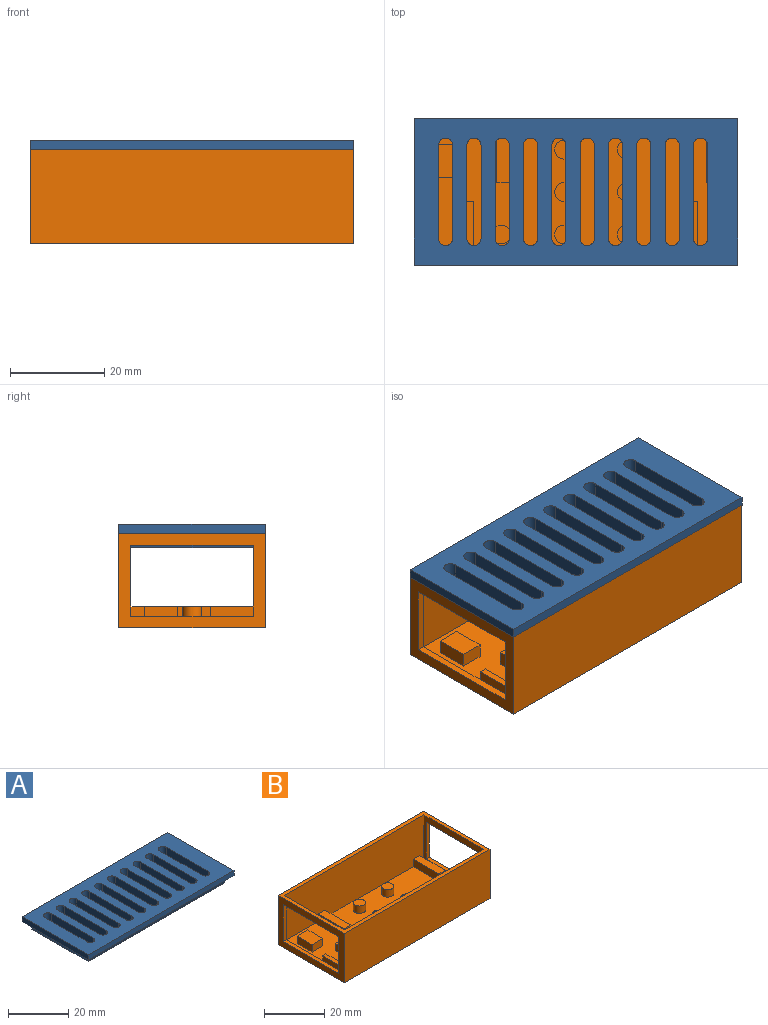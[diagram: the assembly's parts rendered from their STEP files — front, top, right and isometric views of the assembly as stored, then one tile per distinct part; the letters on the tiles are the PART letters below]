
ASSEMBLY  parts=2 mates=1
PART A: 51 faces, bbox 68.5x31x5 mm
  f0: plane 68.5x31mm, normal (0,0,1), area 1458.8mm2, adj f3,f4,f5,f6,f11,f12,f13,f14
  f1: plane 63.89x26.39mm, normal (0,0,-1), area 1021.5mm2, adj f7,f8,f9,f10,f11,f12,f13,f14
  f2: plane 68.5x31mm, normal (0,0,-1), area 289.5mm2, adj f3,f4,f5,f6,f7,f8,f9,f10
  f3: plane 68.5x2mm, normal (0,1,0), area 137mm2, adj f0,f2,f4,f6
  f4: plane 31x2mm, normal (-1,0,0), area 62mm2, adj f0,f2,f3,f5
  f5: plane 68.5x2mm, normal (0,-1,0), area 137mm2, adj f0,f2,f4,f6
  f6: plane 31x2mm, normal (1,0,0), area 62mm2, adj f0,f2,f3,f5
  f7: plane 28x3mm, normal (0.97,0,-0.26), area 84.5mm2, adj f1,f2,f8,f10
  f8: plane 65.5x3mm, normal (0,0.97,-0.26), area 200.9mm2, adj f1,f2,f7,f9
  f9: plane 28x3mm, normal (-0.97,0,-0.26), area 84.5mm2, adj f1,f2,f8,f10
  f10: plane 65.5x3mm, normal (0,-0.97,-0.26), area 200.9mm2, adj f1,f2,f7,f9
  f11: cylinder r=1.5mm len=5mm, axis (0,0,1), area 23.6mm2, adj f0,f1,f12,f14
  f12: plane 19.8x5mm, normal (-1,0,0), area 99mm2, adj f0,f1,f11,f13
  f13: cylinder r=1.5mm len=5mm, axis (0,0,1), area 23.6mm2, adj f0,f1,f12,f14
  f14: plane 19.8x5mm, normal (1,0,0), area 99mm2, adj f0,f1,f11,f13
  f15: cylinder r=1.5mm len=5mm, axis (0,0,1), area 23.6mm2, adj f0,f1,f16,f18
  f16: plane 19.8x5mm, normal (-1,0,0), area 99mm2, adj f0,f1,f15,f17
  f17: cylinder r=1.5mm len=5mm, axis (0,0,1), area 23.6mm2, adj f0,f1,f16,f18
  f18: plane 19.8x5mm, normal (1,0,0), area 99mm2, adj f0,f1,f15,f17
  f19: cylinder r=1.5mm len=5mm, axis (0,0,1), area 23.6mm2, adj f0,f1,f20,f22
  f20: plane 19.8x5mm, normal (-1,0,0), area 99mm2, adj f0,f1,f19,f21
  f21: cylinder r=1.5mm len=5mm, axis (0,0,1), area 23.6mm2, adj f0,f1,f20,f22
  f22: plane 19.8x5mm, normal (1,0,0), area 99mm2, adj f0,f1,f19,f21
  f23: cylinder r=1.5mm len=5mm, axis (0,0,1), area 23.6mm2, adj f0,f1,f24,f26
  f24: plane 19.8x5mm, normal (-1,0,0), area 99mm2, adj f0,f1,f23,f25
  f25: cylinder r=1.5mm len=5mm, axis (0,0,1), area 23.6mm2, adj f0,f1,f24,f26
  f26: plane 19.8x5mm, normal (1,0,0), area 99mm2, adj f0,f1,f23,f25
  f27: cylinder r=1.5mm len=5mm, axis (0,0,1), area 23.6mm2, adj f0,f1,f28,f30
  f28: plane 19.8x5mm, normal (-1,0,0), area 99mm2, adj f0,f1,f27,f29
  f29: cylinder r=1.5mm len=5mm, axis (0,0,1), area 23.6mm2, adj f0,f1,f28,f30
  f30: plane 19.8x5mm, normal (1,0,0), area 99mm2, adj f0,f1,f27,f29
  f31: cylinder r=1.5mm len=5mm, axis (0,0,1), area 23.6mm2, adj f0,f1,f32,f34
  f32: plane 19.8x5mm, normal (-1,0,0), area 99mm2, adj f0,f1,f31,f33
  f33: cylinder r=1.5mm len=5mm, axis (0,0,1), area 23.6mm2, adj f0,f1,f32,f34
  f34: plane 19.8x5mm, normal (1,0,0), area 99mm2, adj f0,f1,f31,f33
  f35: cylinder r=1.5mm len=5mm, axis (0,0,1), area 23.6mm2, adj f0,f1,f36,f38
  f36: plane 19.8x5mm, normal (-1,0,0), area 99mm2, adj f0,f1,f35,f37
  f37: cylinder r=1.5mm len=5mm, axis (0,0,1), area 23.6mm2, adj f0,f1,f36,f38
  f38: plane 19.8x5mm, normal (1,0,0), area 99mm2, adj f0,f1,f35,f37
  f39: cylinder r=1.5mm len=5mm, axis (0,0,1), area 23.6mm2, adj f0,f1,f40,f42
  f40: plane 19.8x5mm, normal (-1,0,0), area 99mm2, adj f0,f1,f39,f41
  f41: cylinder r=1.5mm len=5mm, axis (0,0,1), area 23.6mm2, adj f0,f1,f40,f42
  f42: plane 19.8x5mm, normal (1,0,0), area 99mm2, adj f0,f1,f39,f41
  f43: cylinder r=1.5mm len=5mm, axis (0,0,1), area 23.6mm2, adj f0,f1,f44,f46
  f44: plane 19.8x5mm, normal (-1,0,0), area 99mm2, adj f0,f1,f43,f45
  f45: cylinder r=1.5mm len=5mm, axis (0,0,1), area 23.6mm2, adj f0,f1,f44,f46
  f46: plane 19.8x5mm, normal (1,0,0), area 99mm2, adj f0,f1,f43,f45
  f47: plane 19.8x5mm, normal (1,0,0), area 99mm2, adj f0,f1,f48,f50
  f48: cylinder r=1.5mm len=5mm, axis (0,0,1), area 23.6mm2, adj f0,f1,f47,f49
  f49: plane 19.8x5mm, normal (-1,0,0), area 99mm2, adj f0,f1,f48,f50
  f50: cylinder r=1.5mm len=5mm, axis (0,0,1), area 23.6mm2, adj f0,f1,f47,f49
PART B: 58 faces, bbox 68.5x31x20 mm
  f0: plane 65.5x28mm, normal (0,0,1), area 1552mm2, adj f1,f4,f5,f10,f19,f20,f21,f23
  f1: plane 65.5x18.5mm, normal (0,-1,0), area 1193.7mm2, adj f0,f4,f5,f6,f19,f21,f22,f23
  f2: plane 31x20mm, normal (1,0,0), area 230mm2, adj f6,f7,f8,f9,f15,f16,f17,f18
  f3: plane 31x20mm, normal (-1,0,0), area 230mm2, adj f6,f7,f8,f9,f11,f12,f13,f14
  f4: plane 28x18.5mm, normal (-1,0,0), area 128mm2, adj f0,f1,f6,f10,f15,f16,f17,f18
  f5: plane 28x18.5mm, normal (1,0,0), area 116mm2, adj f0,f1,f6,f10,f11,f12,f13,f14
  f6: plane 68.5x31mm, normal (0,0,1), area 289.5mm2, adj f1,f2,f3,f4,f5,f7,f8,f10
  f7: plane 68.5x20mm, normal (0,1,0), area 1370mm2, adj f2,f3,f6,f9
  f8: plane 68.5x20mm, normal (0,-1,0), area 1370mm2, adj f2,f3,f6,f9
  f9: plane 68.5x31mm, normal (0,0,-1), area 2123.5mm2, adj f2,f3,f7,f8
  f10: plane 65.5x18.5mm, normal (0,1,0), area 1189.2mm2, adj f0,f4,f5,f6,f28,f29,f30,f50
  f11: plane 15x1.5mm, normal (0,-1,0), area 22.5mm2, adj f3,f5,f12,f14
  f12: plane 26x1.5mm, normal (0,0,1), area 39mm2, adj f3,f5,f11,f13,f56
  f13: plane 15x1.5mm, normal (0,1,0), area 22.5mm2, adj f3,f5,f12,f14,f56
  f14: plane 26x1.5mm, normal (0,0,-1), area 39mm2, adj f3,f5,f11,f13
  f15: plane 26x1.5mm, normal (0,0,-1), area 39mm2, adj f2,f4,f16,f18
  f16: plane 15x1.5mm, normal (0,1,0), area 22.5mm2, adj f2,f4,f15,f17
  f17: plane 26x1.5mm, normal (0,0,1), area 39mm2, adj f2,f4,f16,f18
  f18: plane 15x1.5mm, normal (0,-1,0), area 22.5mm2, adj f2,f4,f15,f17
  f19: plane 12x3mm, normal (-1,0,0), area 36mm2, adj f0,f1,f20,f22
  f20: plane 3x3mm, normal (0,-1,0), area 9mm2, adj f0,f19,f21,f22
  f21: plane 12x3mm, normal (1,0,0), area 36mm2, adj f0,f1,f20,f22
  f22: plane 12x3mm, normal (0,0,1), area 36mm2, adj f1,f19,f20,f21
  f23: plane 12x3mm, normal (-1,0,0), area 36mm2, adj f0,f1,f24,f26
  f24: plane 3x3mm, normal (0,-1,0), area 9mm2, adj f0,f23,f25,f26
  f25: plane 12x3mm, normal (1,0,0), area 36mm2, adj f0,f1,f24,f26
  f26: plane 12x3mm, normal (0,0,1), area 36mm2, adj f1,f23,f24,f25
  f27: plane 3x3mm, normal (0,1,0), area 9mm2, adj f0,f28,f29,f30
  f28: plane 12x3mm, normal (-1,0,0), area 36mm2, adj f0,f10,f27,f30
  f29: plane 12x3mm, normal (1,0,0), area 36mm2, adj f0,f10,f27,f30
  f30: plane 12x3mm, normal (0,0,1), area 36mm2, adj f10,f27,f28,f29
  f31: plane 5x3mm, normal (0,1,0), area 15mm2, adj f0,f32,f34,f35
  f32: plane 7x3mm, normal (-1,0,0), area 21mm2, adj f0,f31,f33,f35
  f33: plane 5x3mm, normal (0,-1,0), area 15mm2, adj f0,f32,f34,f35
  f34: plane 7x3mm, normal (1,0,0), area 21mm2, adj f0,f31,f33,f35
  f35: plane 7x5mm, normal (0,0,1), area 35mm2, adj f31,f32,f33,f34
  f36: cylinder r=2mm len=4mm, axis (0,0,-1), area 37.7mm2, adj f0,f37
  f37: plane 4x4mm, normal (0,0,1), area 12.6mm2, adj f36
  f38: cylinder r=2mm len=4mm, axis (0,0,-1), area 37.7mm2, adj f0,f39
  f39: plane 4x4mm, normal (0,0,1), area 12.6mm2, adj f38
  f40: cylinder r=2mm len=4mm, axis (0,0,-1), area 37.7mm2, adj f0,f41
  f41: plane 4x4mm, normal (0,0,1), area 12.6mm2, adj f40
  f42: cylinder r=2mm len=4mm, axis (0,0,-1), area 37.7mm2, adj f0,f43
  f43: plane 4x4mm, normal (0,0,1), area 12.6mm2, adj f42
  f44: cylinder r=2mm len=4mm, axis (0,0,-1), area 37.7mm2, adj f0,f45
  f45: plane 4x4mm, normal (0,0,1), area 12.6mm2, adj f44
  f46: cylinder r=2mm len=4mm, axis (0,0,-1), area 37.7mm2, adj f0,f47
  f47: plane 4x4mm, normal (0,0,1), area 12.6mm2, adj f46
  f48: cylinder r=2mm len=4mm, axis (0,0,-1), area 37.7mm2, adj f0,f49
  f49: plane 4x4mm, normal (0,0,1), area 12.6mm2, adj f48
  f50: plane 12x3mm, normal (1,0,0), area 36mm2, adj f0,f10,f51,f53
  f51: plane 3x3mm, normal (0,1,0), area 9mm2, adj f0,f50,f52,f53
  f52: plane 12x3mm, normal (-1,0,0), area 36mm2, adj f0,f10,f51,f53
  f53: plane 12x3mm, normal (0,0,1), area 36mm2, adj f10,f50,f51,f52
  f54: plane 10x3mm, normal (1,0,0), area 30mm2, adj f0,f10,f55,f57
  f55: plane 3x1.5mm, normal (0,1,0), area 4.5mm2, adj f0,f5,f54,f56,f57
  f56: plane 9x2mm, normal (-1,0,0), area 18mm2, adj f12,f13,f55,f57
  f57: plane 10x1.5mm, normal (0,0,1), area 15mm2, adj f5,f10,f54,f55,f56
PLACE A t=(-1.89,-5.48,16.5)mm
PLACE B t=(2.66,-2.56,-3.5)mm
MATE slider A.f2 <-> B.f6  axis (0,0,-1) through (-31.59,12.94,16.5)mm
